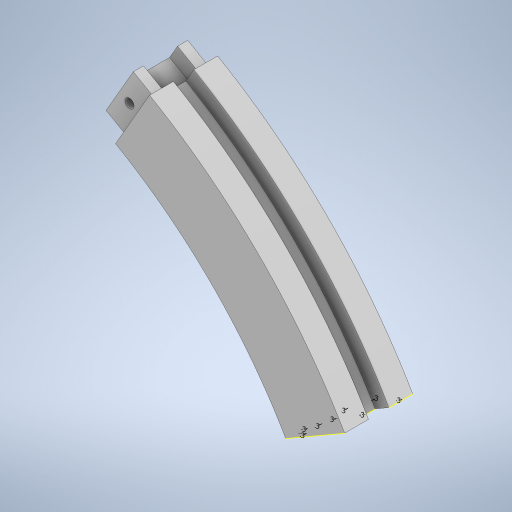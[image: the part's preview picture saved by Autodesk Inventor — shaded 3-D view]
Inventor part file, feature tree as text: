
AUTODESK INVENTOR PART (.ipt)
format: ipt  version: 2023 (Build 270158000, 158)  size: 389,120 bytes
history: native  units: mm
features: sketch x11, extrude x4, plane x4, loft x2, sweep x1
ambient origin geometry x8: Origin, YZ Plane, XZ Plane, XY Plane, X Axis, Y Axis, Z Axis, Center Point
bodies: Body1 (feature_tree)
feature tree (22):
  sweep  "Sweep2"
  extrude  "Extrusion3"  Depth=7.0mm
  extrude  "Extrusion4"  Depth=15.0mm
  sketch  "Sketch9"  dims[d41=220.0mm d42=60.0deg]
  plane  "Work Plane1"
  loft  "Loft1"
  plane  "Work Plane2"
  extrude  "Extrusion5"  TaperAngle=60.0deg  [1 undecoded]
  sketch  "Sketch12"  dims[d48=3.0mm]
  plane  "Work Plane3"
  loft  "Loft2"
  plane  "Work Plane4"
  extrude  "Extrusion6"  Depth=3.0mm
  sketch  "Sketch16"  dims[d51=3.0mm d52=3.0mm d53=3.0mm d54=3.0mm d55=3.0mm d56=10.0mm d57=0.0mm d58=4.0mm d59=12.0mm d60=5.0mm d61=0.0mm d62=0.0mm d63=80.0mm d64=80.0mm d65=40.0mm d66=40.0mm d67=50.0mm d68=30.0mm d69=9.6mm d70=15.0mm d71=31.0mm d72=0.0mm d73=90.0deg d74=0.0mm d75=90.0deg d76=-79.0mm d77=100.0mm d79=140.0mm d80=67.608902mm d81=140.0mm d82=150.0deg d83=50.0mm d84=0.0mm d85=0.0mm d86=5.0mm d87=10.0mm d88=10.0mm d89=10.0mm d90=10.0mm d91=-45.0mm d95=1.0mm d96=1.0mm d97=39.5mm d98=39.5mm d99=0.0mm d100=90.0deg d101=0.0mm d102=90.0deg d103=30.0mm d104=220.0mm d105=30.0deg d107=190.0mm d108=0.0mm d109=0.0mm d110=3.0mm d111=3.0mm d112=3.0mm d113=3.0mm d114=3.0mm d115=3.0mm d116=3.0mm d117=3.0mm]
  sketch  "Sketch2"  dims[d5=100.0mm d18=9.0mm]
  sketch  "Sketch6"  dims[d19=7.0mm d21=16.0mm]
  sketch  "Sketch7"  dims[d22=30.0mm d23=15.0mm]
  sketch  "Sketch8"  dims[d24=4.5mm d25=8.0mm]
  sketch  "Sketch10"  dims[d43=220.0mm d44=0.0mm]
  sketch  "Sketch11"  dims[d45=0.0mm d46=0.0mm d47=3.0mm]
  sketch  "Sketch14"  dims[d49=3.0mm]
  sketch  "Sketch15"  dims[d50=3.0mm]
note: 1 required parameter value undecoded (feature->parameter linkage not recoverable at this tier; creation-order binding heuristic only, values carry confidence <= 0.55)
